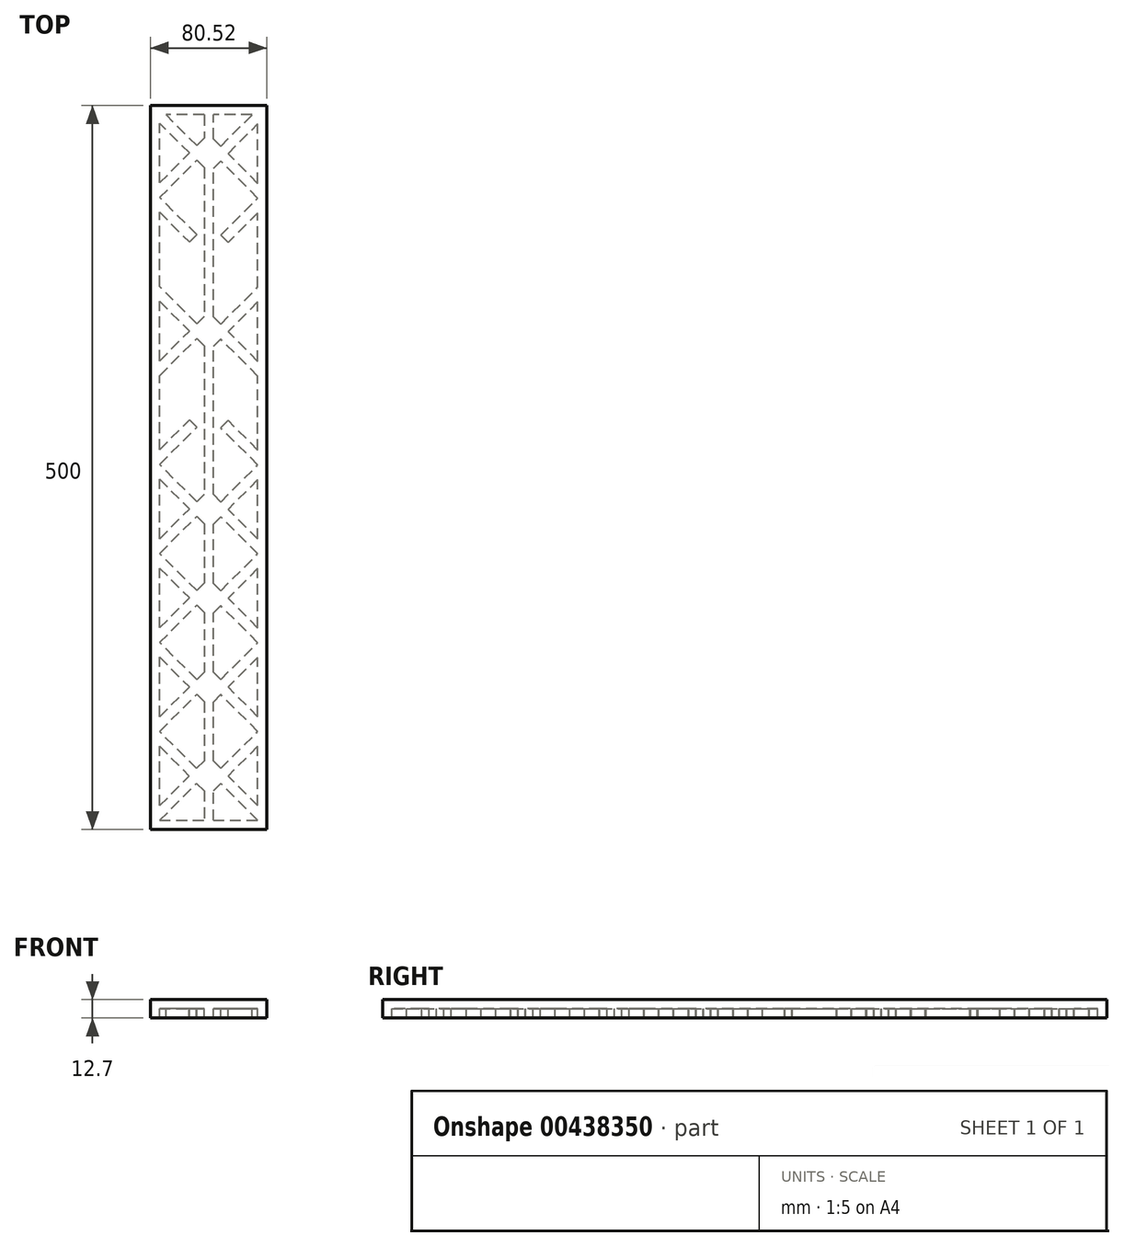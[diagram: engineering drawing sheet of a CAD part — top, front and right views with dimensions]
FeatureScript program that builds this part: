
annotation { "Feature Type Name" : "Feature", "Feature Type Description" : "" }
export const myFeature = defineFeature(function(context is Context, id is Id, definition is map)
    precondition{}
    {
        {
            var Q0;
            Q0=qCreatedBy(makeId("Top.planeOp"),FACE);
            var sketch = newSketch(context, id + "F0", { "sketchPlane" : qUnion([Q0])});
            skLineSegment(sketch, "E0.bottom", {"start": v(0, 480.65) * mm, "end": v(80.52, 480.65) * mm});
            skLineSegment(sketch, "E0.top", {"start": v(0, -19.35) * mm, "end": v(80.52, -19.35) * mm});
            skLineSegment(sketch, "E0.left", {"start": v(0, 480.65) * mm, "end": v(0, -19.35) * mm});
            skLineSegment(sketch, "E0.right", {"start": v(80.52, 480.65) * mm, "end": v(80.52, -19.35) * mm});
            skSolve(sketch);
        }
        {
            var Q0;
            Q0 = qSketchRegion(id + "F0", true);
            extrude(context, id + "F1", {"entities" : qUnion([Q0]), "depth" : 6.35 * mm});
        }
        {
            var Q0;
            Q0=makeQuery(id+"F1.opExtrude","CAP_FACE",FACE,{"disambiguationData":[OSD([sQuery(id+"F0.wireOp",EDGE,"E0.bottom"),sQuery(id+"F0.wireOp",EDGE,"E0.top"),sQuery(id+"F0.wireOp",EDGE,"E0.left"),sQuery(id+"F0.wireOp",EDGE,"E0.right")])],"isStart":true});
            var sketch = newSketch(context, id + "F2", { "sketchPlane" : qUnion([Q0])});
            skLineSegment(sketch, "E1.bottom", {"start": v(0, 19.35) * mm, "end": v(6.35, 19.35) * mm});
            skLineSegment(sketch, "E1.top", {"start": v(0, -480.65) * mm, "end": v(6.35, -480.65) * mm});
            skLineSegment(sketch, "E1.left", {"start": v(0, 19.35) * mm, "end": v(0, -480.65) * mm});
            skLineSegment(sketch, "E1.right", {"start": v(6.35, 19.35) * mm, "end": v(6.35, -480.65) * mm});
            skLineSegment(sketch, "E2.bottom", {"start": v(80.52, 19.35) * mm, "end": v(74.17, 19.35) * mm});
            skLineSegment(sketch, "E2.top", {"start": v(80.52, -480.65) * mm, "end": v(74.17, -480.65) * mm});
            skLineSegment(sketch, "E2.left", {"start": v(80.52, 19.35) * mm, "end": v(80.52, -480.65) * mm});
            skLineSegment(sketch, "E2.right", {"start": v(74.17, 19.35) * mm, "end": v(74.17, -480.65) * mm});
            skLineSegment(sketch, "E3.bottom", {"start": v(6.35, 19.35) * mm, "end": v(74.17, 19.35) * mm});
            skLineSegment(sketch, "E3.top", {"start": v(6.35, 13) * mm, "end": v(74.17, 13) * mm});
            skLineSegment(sketch, "E3.left", {"start": v(6.35, 19.35) * mm, "end": v(6.35, 13) * mm});
            skLineSegment(sketch, "E3.right", {"start": v(74.17, 19.35) * mm, "end": v(74.17, 13) * mm});
            skLineSegment(sketch, "E4.bottom", {"start": v(74.17, -480.65) * mm, "end": v(6.35, -480.65) * mm});
            skLineSegment(sketch, "E4.top", {"start": v(74.17, -474.3) * mm, "end": v(6.35, -474.3) * mm});
            skLineSegment(sketch, "E4.left", {"start": v(74.17, -480.65) * mm, "end": v(74.17, -474.3) * mm});
            skLineSegment(sketch, "E4.right", {"start": v(6.35, -480.65) * mm, "end": v(6.35, -474.3) * mm});
            skSolve(sketch);
        }
        {
            var Q0;
            Q0=makeQuery(id+"F2.imprint","IMPRINT",FACE,{"disambiguationData":[TD([[makeQuery(id+"F2.imprint","IMPRINT",EDGE,{"derivedFrom":sQuery(id+"F2.wireOp",EDGE,"E2.bottom")}),-1.0]])]});
            var Q1;
            Q1=makeQuery(id+"F2.imprint","IMPRINT",FACE,{"disambiguationData":[TD([[makeQuery(id+"F2.imprint","IMPRINT",EDGE,{"derivedFrom":sQuery(id+"F2.wireOp",EDGE,"E1.bottom")}),-1.0]])]});
            var Q2;
            Q2=makeQuery(id+"F2.imprint","IMPRINT",FACE,{"disambiguationData":[TD([[makeQuery(id+"F2.imprint","IMPRINT",EDGE,{"derivedFrom":sQuery(id+"F2.wireOp",EDGE,"E3.bottom")}),-1.0]])]});
            var Q3;
            Q3=makeQuery(id+"F2.imprint","IMPRINT",FACE,{"disambiguationData":[TD([[makeQuery(id+"F2.imprint","IMPRINT",EDGE,{"derivedFrom":sQuery(id+"F2.wireOp",EDGE,"E4.bottom")}),1.0]])]});
            extrude(context, id + "F3", {"entities" : qUnion([Q0, Q1, Q2, Q3]), "operationType" : NewBodyOperationType.ADD, "depth" : 6.35 * mm});
        }
        {
            var Q0;
            Q0=makeQuery(id+"F1.opExtrude","CAP_FACE",FACE,{"disambiguationData":[OSD([sQuery(id+"F0.wireOp",EDGE,"E0.bottom"),sQuery(id+"F0.wireOp",EDGE,"E0.top"),sQuery(id+"F0.wireOp",EDGE,"E0.left"),sQuery(id+"F0.wireOp",EDGE,"E0.right")])],"isStart":true});
            var sketch = newSketch(context, id + "F4", { "sketchPlane" : qUnion([Q0])});
            skLineSegment(sketch, "E5", {"start": v(6.35, 13) * mm, "end": v(37.08, 13) * mm});
            skLineSegment(sketch, "E6", {"start": v(37.08, 13) * mm, "end": v(43.43, 13) * mm});
            skLineSegment(sketch, "E7", {"start": v(43.43, 13) * mm, "end": v(74.17, 13) * mm});
            skLineSegment(sketch, "E8", {"start": v(43.43, 13) * mm, "end": v(43.43, -474.3) * mm});
            skLineSegment(sketch, "E9", {"start": v(43.43, -474.3) * mm, "end": v(37.08, -474.3) * mm});
            skLineSegment(sketch, "E10", {"start": v(37.08, -474.3) * mm, "end": v(37.08, 13) * mm});
            skLineSegment(sketch, "E11", {"start": v(74.17, 13) * mm, "end": v(48.52, -12.62) * mm});
            skLineSegment(sketch, "E12", {"start": v(48.56, -22.81) * mm, "end": v(74.17, -48.39) * mm});
            skLineSegment(sketch, "E13", {"start": v(74.17, -48.39) * mm, "end": v(48.56, -73.96) * mm});
            skLineSegment(sketch, "E14", {"start": v(48.56, -84.2) * mm, "end": v(74.17, -109.77) * mm});
            skLineSegment(sketch, "E15", {"start": v(74.17, -109.77) * mm, "end": v(48.56, -135.34) * mm});
            skLineSegment(sketch, "E16", {"start": v(48.56, -145.58) * mm, "end": v(74.17, -171.15) * mm});
            skLineSegment(sketch, "E17", {"start": v(74.17, -171.15) * mm, "end": v(48.56, -196.73) * mm});
            skLineSegment(sketch, "E18", {"start": v(48.56, -206.96) * mm, "end": v(74.17, -232.53) * mm});
            skLineSegment(sketch, "E19", {"start": v(74.17, -232.53) * mm, "end": v(43.43, -263.22) * mm});
            skLineSegment(sketch, "E20", {"start": v(43.43, -263.22) * mm, "end": v(74.17, -293.91) * mm});
            skLineSegment(sketch, "E21", {"start": v(74.17, -293.91) * mm, "end": v(48.56, -319.49) * mm});
            skLineSegment(sketch, "E22", {"start": v(48.56, -329.72) * mm, "end": v(74.17, -355.3) * mm});
            skLineSegment(sketch, "E23", {"start": v(74.17, -355.3) * mm, "end": v(43.43, -386.07) * mm});
            skLineSegment(sketch, "E24", {"start": v(43.43, -386.07) * mm, "end": v(74.17, -416.76) * mm});
            skLineSegment(sketch, "E25", {"start": v(74.17, -416.76) * mm, "end": v(48.51, -442.45) * mm});
            skLineSegment(sketch, "E26", {"start": v(48.51, -452.61) * mm, "end": v(70.23, -474.3) * mm});
            skLineSegment(sketch, "E27", {"start": v(74.17, 13) * mm, "end": v(74.17, 2.84) * mm});
            skLineSegment(sketch, "E28", {"start": v(74.17, 2.84) * mm, "end": v(53.64, -17.72) * mm});
            skLineSegment(sketch, "E29", {"start": v(74.17, -48.39) * mm, "end": v(74.17, -38.23) * mm});
            skLineSegment(sketch, "E30", {"start": v(74.17, -38.23) * mm, "end": v(53.64, -17.72) * mm});
            skLineSegment(sketch, "E31", {"start": v(74.17, -48.39) * mm, "end": v(74.17, -58.55) * mm});
            skLineSegment(sketch, "E32", {"start": v(74.17, -58.55) * mm, "end": v(53.67, -79.08) * mm});
            skLineSegment(sketch, "E33", {"start": v(74.17, -109.77) * mm, "end": v(74.17, -99.6) * mm});
            skLineSegment(sketch, "E34", {"start": v(74.17, -99.6) * mm, "end": v(53.67, -79.08) * mm});
            skLineSegment(sketch, "E35", {"start": v(74.17, -109.77) * mm, "end": v(74.17, -119.93) * mm});
            skLineSegment(sketch, "E36", {"start": v(74.17, -119.93) * mm, "end": v(53.67, -140.46) * mm});
            skLineSegment(sketch, "E37", {"start": v(74.17, -171.15) * mm, "end": v(74.17, -161) * mm});
            skLineSegment(sketch, "E38", {"start": v(74.17, -161) * mm, "end": v(53.67, -140.46) * mm});
            skLineSegment(sketch, "E39", {"start": v(74.17, -171.15) * mm, "end": v(74.17, -181.31) * mm});
            skLineSegment(sketch, "E40", {"start": v(74.17, -181.31) * mm, "end": v(53.67, -201.84) * mm});
            skLineSegment(sketch, "E41", {"start": v(74.17, -232.53) * mm, "end": v(74.17, -222.37) * mm});
            skLineSegment(sketch, "E42", {"start": v(74.17, -222.37) * mm, "end": v(53.67, -201.84) * mm});
            skLineSegment(sketch, "E43", {"start": v(74.17, -232.53) * mm, "end": v(74.17, -242.7) * mm});
            skLineSegment(sketch, "E44", {"start": v(74.17, -242.7) * mm, "end": v(48.56, -268.34) * mm});
            skLineSegment(sketch, "E45", {"start": v(74.17, -293.91) * mm, "end": v(74.17, -283.75) * mm});
            skLineSegment(sketch, "E46", {"start": v(74.17, -283.75) * mm, "end": v(48.56, -258.1) * mm});
            skLineSegment(sketch, "E47", {"start": v(74.17, -293.91) * mm, "end": v(74.17, -304.07) * mm});
            skLineSegment(sketch, "E48", {"start": v(74.17, -304.07) * mm, "end": v(53.67, -324.6) * mm});
            skLineSegment(sketch, "E49", {"start": v(74.17, -355.3) * mm, "end": v(74.17, -345.14) * mm});
            skLineSegment(sketch, "E50", {"start": v(74.17, -345.14) * mm, "end": v(53.67, -324.6) * mm});
            skLineSegment(sketch, "E51", {"start": v(74.17, -355.3) * mm, "end": v(74.17, -365.46) * mm});
            skLineSegment(sketch, "E52", {"start": v(74.17, -365.46) * mm, "end": v(48.51, -391.15) * mm});
            skLineSegment(sketch, "E53", {"start": v(74.17, -416.76) * mm, "end": v(74.17, -406.6) * mm});
            skLineSegment(sketch, "E54", {"start": v(74.17, -406.6) * mm, "end": v(48.51, -380.99) * mm});
            skLineSegment(sketch, "E55", {"start": v(74.17, -416.76) * mm, "end": v(74.17, -426.92) * mm});
            skLineSegment(sketch, "E56", {"start": v(74.17, -426.92) * mm, "end": v(53.6, -447.53) * mm});
            skLineSegment(sketch, "E57", {"start": v(53.6, -447.53) * mm, "end": v(74.17, -468.07) * mm});
            skLineSegment(sketch, "E58", {"start": v(6.35, 13) * mm, "end": v(31.96, -12.58) * mm});
            skLineSegment(sketch, "E59", {"start": v(31.96, -22.81) * mm, "end": v(6.35, -48.39) * mm});
            skLineSegment(sketch, "E60", {"start": v(6.35, 13) * mm, "end": v(6.35, 2.84) * mm});
            skLineSegment(sketch, "E61", {"start": v(6.35, 2.84) * mm, "end": v(26.85, -17.7) * mm});
            skLineSegment(sketch, "E62", {"start": v(6.35, -48.39) * mm, "end": v(6.35, -38.23) * mm});
            skLineSegment(sketch, "E63", {"start": v(6.35, -38.23) * mm, "end": v(26.85, -17.7) * mm});
            skLineSegment(sketch, "E64", {"start": v(6.35, -48.39) * mm, "end": v(32, -74.08) * mm});
            skLineSegment(sketch, "E65", {"start": v(32, -84.24) * mm, "end": v(6.35, -109.85) * mm});
            skLineSegment(sketch, "E66", {"start": v(6.35, -109.85) * mm, "end": v(32, -135.54) * mm});
            skLineSegment(sketch, "E67", {"start": v(32, -145.7) * mm, "end": v(6.35, -171.32) * mm});
            skLineSegment(sketch, "E68", {"start": v(6.35, -171.32) * mm, "end": v(32, -197.01) * mm});
            skLineSegment(sketch, "E69", {"start": v(32, -207.17) * mm, "end": v(6.35, -232.8) * mm});
            skLineSegment(sketch, "E70", {"start": v(6.35, -232.8) * mm, "end": v(37.08, -263.57) * mm});
            skLineSegment(sketch, "E71", {"start": v(37.08, -263.57) * mm, "end": v(6.35, -294.26) * mm});
            skLineSegment(sketch, "E72", {"start": v(6.35, -294.26) * mm, "end": v(32, -319.95) * mm});
            skLineSegment(sketch, "E73", {"start": v(32, -330.1) * mm, "end": v(6.35, -355.73) * mm});
            skLineSegment(sketch, "E74", {"start": v(6.35, -355.73) * mm, "end": v(37.08, -386.5) * mm});
            skLineSegment(sketch, "E75", {"start": v(37.08, -386.5) * mm, "end": v(6.35, -417.2) * mm});
            skLineSegment(sketch, "E76", {"start": v(6.35, -417.2) * mm, "end": v(32, -442.89) * mm});
            skLineSegment(sketch, "E77", {"start": v(32, -453.05) * mm, "end": v(10.72, -474.3) * mm});
            skLineSegment(sketch, "E78", {"start": v(6.35, -417.2) * mm, "end": v(6.35, -427.36) * mm});
            skLineSegment(sketch, "E79", {"start": v(6.35, -427.36) * mm, "end": v(26.92, -447.96) * mm});
            skLineSegment(sketch, "E80", {"start": v(26.92, -447.96) * mm, "end": v(6.35, -468.5) * mm});
            skLineSegment(sketch, "E81", {"start": v(6.35, -417.2) * mm, "end": v(6.35, -407.04) * mm});
            skLineSegment(sketch, "E82", {"start": v(6.35, -407.04) * mm, "end": v(32, -381.42) * mm});
            skLineSegment(sketch, "E83", {"start": v(6.35, -355.73) * mm, "end": v(6.35, -365.89) * mm});
            skLineSegment(sketch, "E84", {"start": v(6.35, -365.89) * mm, "end": v(32, -391.58) * mm});
            skLineSegment(sketch, "E85", {"start": v(6.35, -355.73) * mm, "end": v(6.35, -345.57) * mm});
            skLineSegment(sketch, "E86", {"start": v(6.35, -345.57) * mm, "end": v(26.92, -325.02) * mm});
            skLineSegment(sketch, "E87", {"start": v(6.35, -294.26) * mm, "end": v(6.35, -304.42) * mm});
            skLineSegment(sketch, "E88", {"start": v(6.35, -304.42) * mm, "end": v(26.92, -325.02) * mm});
            skLineSegment(sketch, "E89", {"start": v(6.35, -294.26) * mm, "end": v(6.35, -284.1) * mm});
            skLineSegment(sketch, "E90", {"start": v(6.35, -284.1) * mm, "end": v(32, -258.48) * mm});
            skLineSegment(sketch, "E91", {"start": v(6.35, -232.8) * mm, "end": v(6.35, -242.95) * mm});
            skLineSegment(sketch, "E92", {"start": v(6.35, -242.95) * mm, "end": v(32, -268.64) * mm});
            skLineSegment(sketch, "E93", {"start": v(6.35, -232.8) * mm, "end": v(6.35, -222.63) * mm});
            skLineSegment(sketch, "E94", {"start": v(6.35, -222.63) * mm, "end": v(26.92, -202.09) * mm});
            skLineSegment(sketch, "E95", {"start": v(6.35, -171.32) * mm, "end": v(6.35, -181.48) * mm});
            skLineSegment(sketch, "E96", {"start": v(6.35, -181.48) * mm, "end": v(26.92, -202.09) * mm});
            skLineSegment(sketch, "E97", {"start": v(6.35, -171.32) * mm, "end": v(6.35, -161.16) * mm});
            skLineSegment(sketch, "E98", {"start": v(6.35, -161.16) * mm, "end": v(26.92, -140.62) * mm});
            skLineSegment(sketch, "E99", {"start": v(6.35, -109.85) * mm, "end": v(6.35, -120.01) * mm});
            skLineSegment(sketch, "E100", {"start": v(6.35, -120.01) * mm, "end": v(26.92, -140.62) * mm});
            skLineSegment(sketch, "E101", {"start": v(6.35, -109.85) * mm, "end": v(6.35, -99.7) * mm});
            skLineSegment(sketch, "E102", {"start": v(6.35, -99.7) * mm, "end": v(26.92, -79.15) * mm});
            skLineSegment(sketch, "E103", {"start": v(6.35, -48.39) * mm, "end": v(6.35, -58.55) * mm});
            skLineSegment(sketch, "E104", {"start": v(6.35, -58.55) * mm, "end": v(26.92, -79.15) * mm});
            skLineSegment(sketch, "E105", {"start": v(32, -145.7) * mm, "end": v(37.08, -150.8) * mm});
            skLineSegment(sketch, "E106", {"start": v(32, -135.54) * mm, "end": v(37.08, -130.47) * mm});
            skLineSegment(sketch, "E107", {"start": v(32, -84.24) * mm, "end": v(37.08, -89.32) * mm});
            skLineSegment(sketch, "E108", {"start": v(32, -74.08) * mm, "end": v(37.08, -69) * mm});
            skLineSegment(sketch, "E109", {"start": v(31.96, -12.58) * mm, "end": v(37.08, -7.45) * mm});
            skLineSegment(sketch, "E110", {"start": v(31.96, -22.81) * mm, "end": v(37.08, -27.94) * mm});
            skLineSegment(sketch, "E111", {"start": v(32, -197.01) * mm, "end": v(37.08, -191.94) * mm});
            skLineSegment(sketch, "E112", {"start": v(32, -207.17) * mm, "end": v(37.08, -212.26) * mm});
            skLineSegment(sketch, "E113", {"start": v(32, -258.48) * mm, "end": v(37.08, -253.4) * mm});
            skLineSegment(sketch, "E114", {"start": v(32, -268.64) * mm, "end": v(37.08, -273.73) * mm});
            skLineSegment(sketch, "E115", {"start": v(32, -319.95) * mm, "end": v(37.08, -314.88) * mm});
            skLineSegment(sketch, "E116", {"start": v(32, -330.1) * mm, "end": v(37.08, -335.2) * mm});
            skLineSegment(sketch, "E117", {"start": v(32, -381.42) * mm, "end": v(37.08, -376.34) * mm});
            skLineSegment(sketch, "E118", {"start": v(32, -391.58) * mm, "end": v(37.08, -396.66) * mm});
            skLineSegment(sketch, "E119", {"start": v(32, -442.89) * mm, "end": v(37.08, -437.81) * mm});
            skLineSegment(sketch, "E120", {"start": v(32, -453.05) * mm, "end": v(37.08, -458.13) * mm});
            skLineSegment(sketch, "E121", {"start": v(48.51, -452.61) * mm, "end": v(43.43, -457.69) * mm});
            skLineSegment(sketch, "E122", {"start": v(48.51, -442.45) * mm, "end": v(43.43, -437.38) * mm});
            skLineSegment(sketch, "E123", {"start": v(48.51, -391.15) * mm, "end": v(43.43, -396.23) * mm});
            skLineSegment(sketch, "E124", {"start": v(48.51, -380.99) * mm, "end": v(43.43, -375.91) * mm});
            skLineSegment(sketch, "E125", {"start": v(48.56, -329.72) * mm, "end": v(43.43, -334.85) * mm});
            skLineSegment(sketch, "E126", {"start": v(48.56, -319.49) * mm, "end": v(43.43, -314.36) * mm});
            skLineSegment(sketch, "E127", {"start": v(48.56, -268.34) * mm, "end": v(43.43, -273.47) * mm});
            skLineSegment(sketch, "E128", {"start": v(48.56, -258.1) * mm, "end": v(43.43, -252.98) * mm});
            skLineSegment(sketch, "E129", {"start": v(48.56, -206.96) * mm, "end": v(43.43, -212.09) * mm});
            skLineSegment(sketch, "E130", {"start": v(48.56, -196.73) * mm, "end": v(43.43, -191.6) * mm});
            skLineSegment(sketch, "E131", {"start": v(48.56, -145.58) * mm, "end": v(43.43, -150.7) * mm});
            skLineSegment(sketch, "E132", {"start": v(48.56, -135.34) * mm, "end": v(43.43, -130.21) * mm});
            skLineSegment(sketch, "E133", {"start": v(48.56, -84.2) * mm, "end": v(43.43, -89.32) * mm});
            skLineSegment(sketch, "E134", {"start": v(48.56, -73.96) * mm, "end": v(43.43, -68.83) * mm});
            skLineSegment(sketch, "E135", {"start": v(48.56, -22.81) * mm, "end": v(43.43, -27.94) * mm});
            skLineSegment(sketch, "E136", {"start": v(48.52, -12.62) * mm, "end": v(43.43, -7.52) * mm});
            skPoint(sketch, "E137.orphan", {"position": v(43.43, -447.54) * mm});
            skPoint(sketch, "E138.orphan", {"position": v(43.43, -324.6) * mm});
            skSolve(sketch);
        }
        {
            var Q0;
            {var subQ34=sQuery(id+"F4.wireOp",EDGE,"E6");Q0=makeQuery(id+"F4.imprint","IMPRINT",FACE,{"disambiguationData":[TD([[makeQuery(id+"F4.imprint","IMPRINT",EDGE,{"derivedFrom":subQ34}),-1.0]])]});}
            var Q1;
            {var subQ0=sQuery(id+"F4.wireOp",EDGE,"E49");Q1=makeQuery(id+"F4.imprint","IMPRINT",FACE,{"disambiguationData":[TD([[makeQuery(id+"F4.imprint","IMPRINT",EDGE,{"derivedFrom":subQ0}),-1.0]])]});}
            var Q2;
            {var subQ1=makeQuery(id+"F3.opExtrude","CAP_EDGE",EDGE,{"disambiguationData":[OSD([sQuery(id+"F2.wireOp",EDGE,"E2.right")])],"isStart":true});var subQ3=sQuery(id+"F4.wireOp",EDGE,"E57");var subQ4=makeQuery(id+"F4.imprint","INTERSECT",VERTEX,{"derivedFrom":[subQ1,subQ3]});Q2=makeQuery(id+"F4.imprint","IMPRINT",FACE,{"disambiguationData":[TD([[makeQuery(id+"F4.imprint","IMPRINT",EDGE,{"disambiguationData":[TD([[subQ4,1.0]])],"derivedFrom":subQ3}),-1.0]])]});}
            var Q3;
            {var subQ0=sQuery(id+"F4.wireOp",EDGE,"E80");var subQ1=makeQuery(id+"F3.opExtrude","CAP_EDGE",EDGE,{"disambiguationData":[OSD([sQuery(id+"F2.wireOp",EDGE,"E1.right")])],"isStart":true});var subQ2=makeQuery(id+"F4.imprint","INTERSECT",VERTEX,{"derivedFrom":[subQ1,subQ0]});Q3=makeQuery(id+"F4.imprint","IMPRINT",FACE,{"disambiguationData":[TD([[makeQuery(id+"F4.imprint","IMPRINT",EDGE,{"disambiguationData":[TD([[subQ2,1.0]])],"derivedFrom":subQ0}),1.0]])]});}
            var Q4;
            {var subQ0=sQuery(id+"F4.wireOp",EDGE,"KKNoya52-zN26-vuy2-JsY4-ziXRhTCN7kHm");Q4=makeQuery(id+"F4.imprint","IMPRINT",FACE,{"disambiguationData":[TD([[makeQuery(id+"F4.imprint","IMPRINT",EDGE,{"derivedFrom":subQ0}),-1.0]])]});}
            var Q5;
            {var subQ0=sQuery(id+"F4.wireOp",EDGE,"ZSV6ituq-rJHO-S46Q-9mIa-q0AfQFWMdoCt");Q5=makeQuery(id+"F4.imprint","IMPRINT",FACE,{"disambiguationData":[TD([[makeQuery(id+"F4.imprint","IMPRINT",EDGE,{"derivedFrom":subQ0}),1.0]])]});}
            var Q6;
            {var subQ0=sQuery(id+"F4.wireOp",EDGE,"E81");Q6=makeQuery(id+"F4.imprint","IMPRINT",FACE,{"disambiguationData":[TD([[makeQuery(id+"F4.imprint","IMPRINT",EDGE,{"derivedFrom":subQ0}),1.0]])]});}
            var Q7;
            {var subQ0=sQuery(id+"F4.wireOp",EDGE,"E53");Q7=makeQuery(id+"F4.imprint","IMPRINT",FACE,{"disambiguationData":[TD([[makeQuery(id+"F4.imprint","IMPRINT",EDGE,{"derivedFrom":subQ0}),-1.0]])]});}
            var Q8;
            {var subQ0=sQuery(id+"F4.wireOp",EDGE,"E41");Q8=makeQuery(id+"F4.imprint","IMPRINT",FACE,{"disambiguationData":[TD([[makeQuery(id+"F4.imprint","IMPRINT",EDGE,{"derivedFrom":subQ0}),-1.0]])]});}
            var Q9;
            {var subQ0=sQuery(id+"F4.wireOp",EDGE,"E43");Q9=makeQuery(id+"F4.imprint","IMPRINT",FACE,{"disambiguationData":[TD([[makeQuery(id+"F4.imprint","IMPRINT",EDGE,{"derivedFrom":subQ0}),-1.0]])]});}
            var Q10;
            {var subQ0=sQuery(id+"F4.wireOp",EDGE,"E85");Q10=makeQuery(id+"F4.imprint","IMPRINT",FACE,{"disambiguationData":[TD([[makeQuery(id+"F4.imprint","IMPRINT",EDGE,{"derivedFrom":subQ0}),1.0]])]});}
            var Q11;
            {var subQ0=sQuery(id+"F4.wireOp",EDGE,"E91");Q11=makeQuery(id+"F4.imprint","IMPRINT",FACE,{"disambiguationData":[TD([[makeQuery(id+"F4.imprint","IMPRINT",EDGE,{"derivedFrom":subQ0}),1.0]])]});}
            extrude(context, id + "F5", {"entities" : qUnion([Q0, Q1, Q2, Q3, Q4, Q5, Q6, Q7, Q8, Q9, Q10, Q11]), "operationType" : NewBodyOperationType.ADD, "depth" : 6.35 * mm});
        }
        {
            var Q0;
            Q0=makeQuery(id+"F4.imprint","IMPRINT",FACE,{"disambiguationData":[TD([[makeQuery(id+"F4.imprint","IMPRINT",EDGE,{"derivedFrom":sQuery(id+"F4.wireOp",EDGE,"E66")}),-1.0]])]});
            var Q1;
            Q1=makeQuery(id+"F4.imprint","IMPRINT",FACE,{"disambiguationData":[TD([[makeQuery(id+"F4.imprint","IMPRINT",EDGE,{"derivedFrom":sQuery(id+"F4.wireOp",EDGE,"E15")}),1.0]])]});
            var Q2;
            Q2=makeQuery(id+"F4.imprint","IMPRINT",FACE,{"disambiguationData":[TD([[makeQuery(id+"F4.imprint","IMPRINT",EDGE,{"derivedFrom":sQuery(id+"F4.wireOp",EDGE,"E58")}),-1.0]])]});
            var Q3;
            Q3=makeQuery(id+"F4.imprint","IMPRINT",FACE,{"disambiguationData":[TD([[makeQuery(id+"F4.imprint","IMPRINT",EDGE,{"derivedFrom":sQuery(id+"F4.wireOp",EDGE,"E11")}),1.0]])]});
            var Q4;
            Q4=makeQuery(id+"F4.imprint","IMPRINT",FACE,{"disambiguationData":[TD([[makeQuery(id+"F4.imprint","IMPRINT",EDGE,{"derivedFrom":sQuery(id+"F4.wireOp",EDGE,"E13")}),1.0]])]});
            extrude(context, id + "F6", {"entities" : qUnion([Q0, Q1, Q2, Q3, Q4]), "operationType" : NewBodyOperationType.ADD, "depth" : 6.35 * mm});
        }
        {
            var Q0;
            Q0=makeQuery(id+"F4.imprint","IMPRINT",FACE,{"disambiguationData":[TD([[makeQuery(id+"F4.imprint","IMPRINT",EDGE,{"derivedFrom":sQuery(id+"F4.wireOp",EDGE,"E64")}),-1.0]])]});
            var Q1;
            Q1=makeQuery(id+"F4.imprint","IMPRINT",FACE,{"disambiguationData":[TD([[makeQuery(id+"F4.imprint","IMPRINT",EDGE,{"derivedFrom":sQuery(id+"F4.wireOp",EDGE,"E68")}),-1.0]])]});
            extrude(context, id + "F7", {"entities" : qUnion([Q0, Q1]), "operationType" : NewBodyOperationType.ADD, "depth" : 6.35 * mm});
        }
    });
